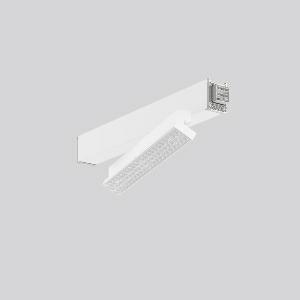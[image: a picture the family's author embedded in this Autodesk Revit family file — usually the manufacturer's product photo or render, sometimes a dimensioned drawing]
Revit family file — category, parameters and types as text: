
# Revit family: linedo_strahlermodule_-_tx-move_950690_842_476_300_801d
name_source: partatom
category: Lighting Fixtures
units: mm (PartAtom-declared; Revit-internal decimal feet)

## family parameters
Cut with Voids When Loaded = No
Host = Face
Light Source = No
Part Type = Normal
Room Calculation Point = No
Round Connector Dimension = Use Diameter
Shared = No

## types (1)
- MultiLumen 1 (1 x LED Modul 840, 2900 lm, 4000)
    Apparent Load = 19 VA
    CIE Flux Codes = 77 96 99 100 100
    Color Rendering = 80
    Color Temperature = 4000
    Default Elevation = 1800 mm
    Description = LINEDO, 19. 40 W, 2900. 5550 lm, 840, white, DALI
Continuous line luminaire, L 598 B 58 H 131
    Height = 131 mm
    Lamp = 1 x LED Modul 840
    Lamp Light Flux = 2900 lm
    Lamp count = 1
    Length = 598 mm
    Lifetime = 50000 h
    Luminous efficacy = 153 lm/W
    Manufacturer = RZB
    ModVariant = No
    Model = 950690.842.476.300
    Mounting Place = Ceiling
    Mounting Type = Surface mounted
    Number of Poles = 1
    OnlyDefault = Yes
    Power Factor = 1
    Product Name = LINEDO Strahlermodule - TX-MOVE
    Product group = Surface mounted continuous line luminaire system
    ProductGroupID = 310
    Protection Class = Protection class I
    Protection Degree = Degree of protection
    RLX_Detail_Level = 1
    RLX_Emergency_Light_Flux = 0 lm
    RLX_Emergency_Type = 0
    RLX_Emergency_Type_DB = No
    RlxData = <blob elided: 22965 chars, md5=3130ca65>
    Socket = socket
    Standby Power = 0 W
    System Light Flux = 2900 lm
    System Power = 19 W
    Type Comments = MultiLumen 1
    Type Image = 950690.842.476.300.jpg
    URL = http://relux.com
    VarID = multilumen_1
    Voltage = 0 V
    Weight = 0.00 kg
    Width = 58 mm

## geometry (parser evidence)
native form markers: Blend x4, Sweep x18
no freeform markers — native parametric forms only
